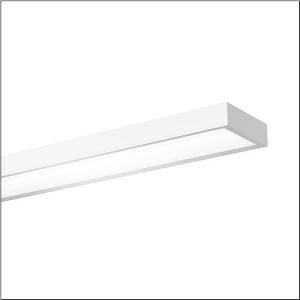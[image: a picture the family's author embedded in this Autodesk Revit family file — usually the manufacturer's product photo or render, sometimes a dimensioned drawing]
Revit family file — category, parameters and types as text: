
# Revit family: sport_31_51hs12dc4dca
name_source: partatom
category: Lighting Fixtures
units: mm (PartAtom-declared; Revit-internal decimal feet)

## family parameters
Cut with Voids When Loaded = No
Host = Face
Light Source = No
Part Type = Normal
Room Calculation Point = No
Round Connector Dimension = Use Diameter
Shared = No

## types (1)
- --- (1 x LED, 8000 lm, 59.4 W, 4000K)
    Apparent Load = 59 VA
    CIE Flux Codes = 65 89 97 100 100
    Color Rendering = 80
    Color Temperature = 4000K
    Default Elevation = 1800 mm
    Description = Sport 31, LED high bay luminaire, primary light control with reflector, of sheet steel, primary anti-glare with prismatic structure, of PC, primary optical cover: cover panel, of PC, light emission: direct distribution, primary light characteristic: symmetric, installation type: suspended mounting, recessed, surface-mounted, LED, rated luminous flux: 8.000lm, luminous efficacy: 135lm/W, light colour: 840, colour temperature: 4000K, control gear: ECG DALI, with terminal, 5-pole, max. 2.5mm², mains connection: 220..240V, AC/DC, 50/60Hz, rated input power: 58W, housing, of sheet steel, traffic white (RAL 9016), length: 1.540mm, width: 315mm, height: 95mm, protection rating (complete): IP20, protection rating (lamp compartment, on room side): IP50, insulation class (complete): insulation class I (protective earthing), certification: CE, ENEC, UKCA, ball protection: ball impact resistant with ceiling mounting or chain suspension, impact resistance: IK08, permissible operating ambient temperature: -20..+35°C, standard: DIN 18032-3, EN 60598-2-22, packaging unit: 1 piece
    Height = 100 mm  [stored 0.328084 ft]
    Lamp = 1 x LED
    Lamp Light Flux = 8000 lm
    Lamp Power = 59.4 W
    Lamp count = 1
    Length = 1500 mm
    Luminous efficacy = 135 lm/W
    Manufacturer = Siteco
    ModVariant = No
    Model = 51HS12DC4DCA
    Mounting Place = Ceiling
    Mounting Type = Pendant
    Number of Poles = 1
    OnlyDefault = Yes
    Power Factor = 1
    Product Name = Sport 31
    Product group = LED high bay luminaire
    ProductGroupID = 903
    Protection Class = Protection class I
    Protection Degree = IP 20
    RLX_Detail_Level = 1
    RLX_Emergency_Light_Flux = 0 lm
    RLX_Emergency_Type = 0
    RLX_Emergency_Type_DB = No
    RlxData = <blob elided: 22813 chars, md5=9fdfee1e>
    Socket = socket
    Standby Power = 0 W
    System Light Flux = 8000 lm
    System Power = 59 W
    Type Comments = factory setting: luminous flux: 100 % | dim-lin: 254 | 247 mA
    Type Image = l_1006823.jpg
    URL = http://relux.com
    VarID = @adj_133089
    Voltage = 0 V
    Weight = 0.00 kg
    Width = 315 mm

note: [stored X ft] marks values corroborated as IEEE doubles in the binary element streams (Revit-internal decimal feet)

## geometry (parser evidence)
native form markers: Blend x4, Sweep x10
no freeform markers — native parametric forms only
